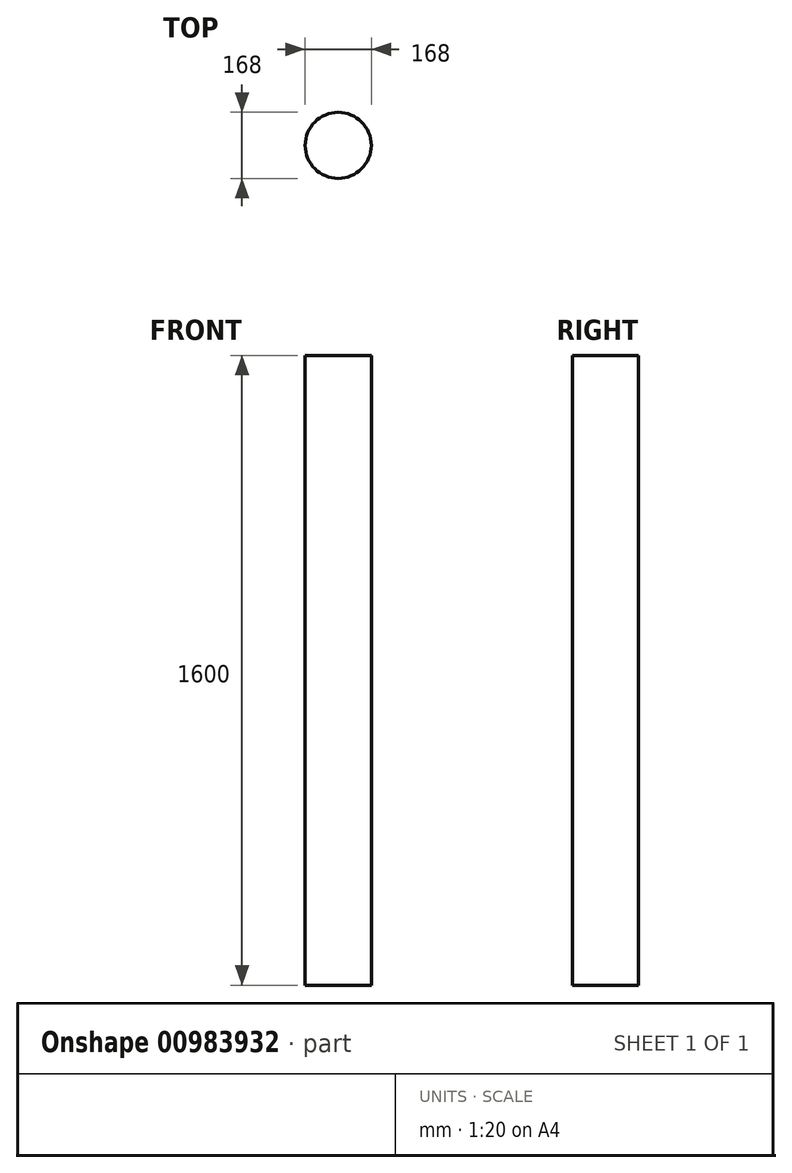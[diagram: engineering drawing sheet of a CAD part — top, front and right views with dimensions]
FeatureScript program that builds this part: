
annotation { "Feature Type Name" : "Feature", "Feature Type Description" : "" }
export const myFeature = defineFeature(function(context is Context, id is Id, definition is map)
    precondition{}
    {
        {
            var Q0;
            Q0=qCreatedBy(makeId("Top.planeOp"),FACE);
            var sketch = newSketch(context, id + "F0", { "sketchPlane" : qUnion([Q0])});
            skCircle(sketch, "E0", {"center": v(0, 0) * mm, "radius": 84 * mm});
            skSolve(sketch);
        }
        {
            var Q0;
            Q0=makeQuery(id+"F0.imprint","IMPRINT",FACE,{"disambiguationData":[TD([[makeQuery(id+"F0.imprint","IMPRINT",EDGE,{"derivedFrom":sQuery(id+"F0.wireOp",EDGE,"E0")}),1.0]])]});
            extrude(context, id + "F1", {"entities" : qUnion([Q0]), "depth" : 1600 * mm, "offsetDistance" : 25 * mm});
        }
    });
